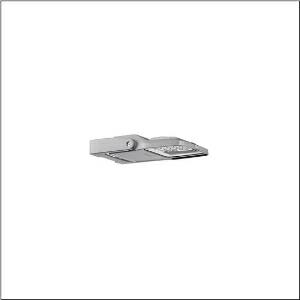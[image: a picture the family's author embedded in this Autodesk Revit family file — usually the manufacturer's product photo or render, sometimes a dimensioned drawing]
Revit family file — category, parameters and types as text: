
# Revit family: floodlight_fl_21_iq_micro___pl61_5xa7761a4c2a_08ca
name_source: partatom
category: Lighting Fixtures
units: mm (PartAtom-declared; Revit-internal decimal feet)

## family parameters
Cut with Voids When Loaded = No
Host = Face
Light Source = No
Part Type = Normal
Room Calculation Point = No
Round Connector Dimension = Use Diameter
Shared = No

## types (1)
- --- (1 x LED, 3030 lm, 23.1 W, 4000K)
    Apparent Load = 23 VA
    CIE Flux Codes = 33 65 98 100 100
    Color Rendering = 70
    Color Temperature = 4000K
    Default Elevation = 1800 mm
    Description = Floodlight FL 21 iQ micro, floodlight, primary light control with lens, of PMMA, primary optical cover: protective disc, of toughened safety glass, transparent, light distribution: PL61, light emission: direct distribution, installation type: surface-mounted, lamps: LED, High Power LED, rated values: 3.030lm | 23,1W | 131,2lm/W (begin service life); end service life: 3.030lm | 23,8W; at 50% lumin. flux: 1.515lm | 11W | 137,7lm/W, colour temperature: 4000K, colour rendering: CRI > 70, light colour: 740, light setting 1 begin service life: 100% | 3.030lm | 23,1W | 131,2lm/W | 4.000K, light setting 1 end service life: 23,8W, further light settings possible, control: optimised constant luminous flux control (CLO 2.0), Desk-Remote (wireless, voltage-free reading and setting of iQ features in the workshop via application-optimized NFC function/RFID function), Light-Fading, Smart-Wire, Night-Set, Lumen-Switch, Temp-Guard, Auto-Match, pre-setting: linear dimming characteristic, with terminal, 6-pole, mains connection: 220..240V, AC, 50/60Hz, luminaire housing, of diecast aluminium, powder-coated, SITECO metallic grey (DB 702S), corrosivity category C5 mid according to DIN EN ISO 12944suitable for swimming poolschlorine-resistant, sealing non-destructively replaceable, design bracket, of diecast aluminium, powder-coated, SITECO metallic grey (DB 702S), protection rating (complete): IP66, insulation class (complete): insulation class II (safety insulation), certification: CE, ENEC, VDE, protection symbol: D, impact resistance: IK07, permissible operating ambient temperature: -40..+40°C, permissible operating ambient temperature for outdoor applications: -40..+50°C, standard: DIN EN 12944, LABS conformity tested according to VDMA 24364:2018-05, packaging unit: 1 piece

Light Distribution: PL61
    Height = 65 mm
    Lamp = 1 x LED
    Lamp Light Flux = 3030 lm
    Lamp Power = 23.1 W
    Lamp count = 1
    Length = 312 mm
    Luminous efficacy = 131 lm/W
    Manufacturer = Siteco
    ModVariant = No
    Model = 5XA7761A4C2A
    Mounting Place = Wall
    Mounting Type = Surface mounted
    Number of Poles = 1
    OnlyDefault = Yes
    Power Factor = 1
    Product Name = Floodlight FL 21 iQ micro | PL61
    Product group = floodlight | wall mounted
    ProductGroupID = 2002
    Protection Class = Protection class II
    Protection Degree = IP 66
    RLX_Detail_Level = 1
    RLX_Emergency_Light_Flux = 0 lm
    RLX_Emergency_Type = 0
    RLX_Emergency_Type_DB = No
    RlxData = <blob elided: 97869 chars, md5=e2c918e5>
    Socket = socket
    Standby Power = 0 W
    System Light Flux = 3030 lm
    System Power = 23 W
    Type Comments = factory setting: luminous flux: 100 % | dim-lin: 254 | 455 mA
    Type Image = l_1006878.jpg
    URL = http://relux.com
    VarID = @adj_192013
    Voltage = 0 V
    Weight = 0.00 kg
    Width = 230 mm

## geometry (parser evidence)
native form markers: Blend x4, Sweep x14
no freeform markers — native parametric forms only
